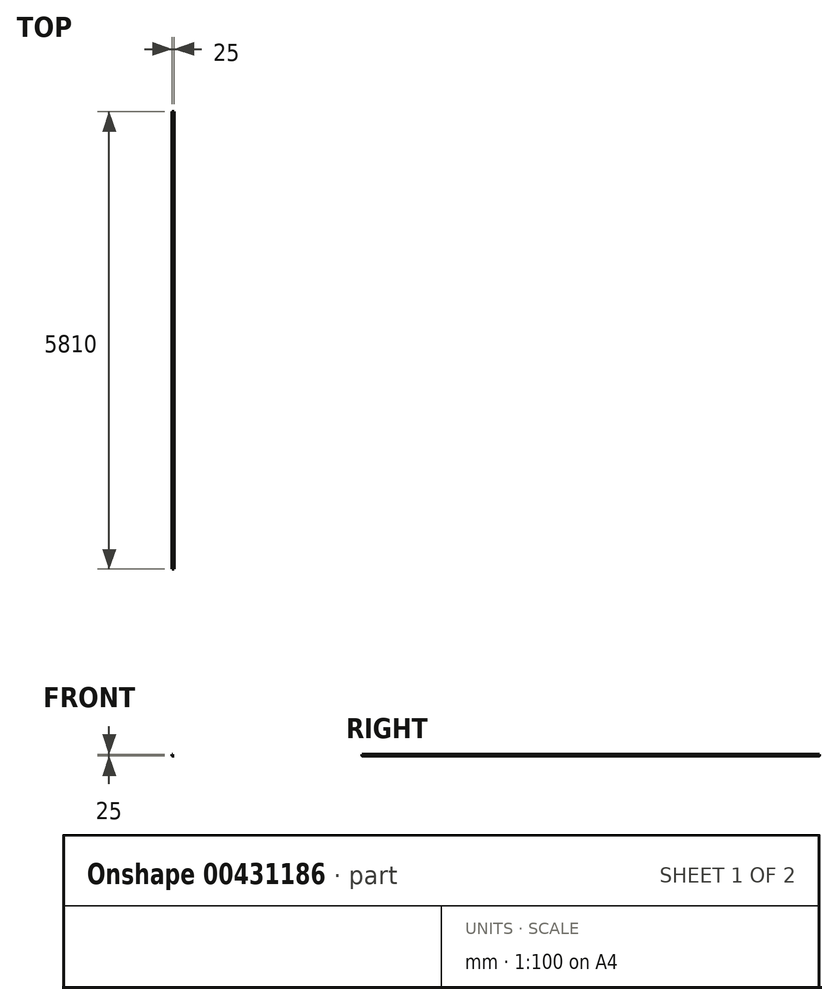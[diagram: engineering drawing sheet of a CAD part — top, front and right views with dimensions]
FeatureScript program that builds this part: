
annotation { "Feature Type Name" : "Feature", "Feature Type Description" : "" }
export const myFeature = defineFeature(function(context is Context, id is Id, definition is map)
    precondition{}
    {
        {
            var Q0;
            Q0=qCreatedBy(makeId("Front.planeOp"),FACE);
            var sketch = newSketch(context, id + "F0", { "sketchPlane" : qUnion([Q0])});
            skLineSegment(sketch, "E0", {"start": v(4.6, 0) * mm, "end": v(25, 0) * mm});
            skLineSegment(sketch, "E1", {"start": v(0, 4.6) * mm, "end": v(0, 25) * mm});
            skLineSegment(sketch, "E2.0", {"start": v(2.3, 4.6) * mm, "end": v(2.3, 25) * mm});
            skLineSegment(sketch, "E3.0", {"start": v(4.6, 2.3) * mm, "end": v(25, 2.3) * mm});
            skLineSegment(sketch, "E4", {"start": v(25, 0) * mm, "end": v(25, 2.3) * mm});
            skLineSegment(sketch, "E5", {"start": v(0, 25) * mm, "end": v(2.3, 25) * mm});
            skPoint(sketch, "E6.visualSharp", {"position": v(2.3, 2.3) * mm});
            skArc(sketch, "E6.filletArc", {"start": v(2.3, 4.6) * mm, "mid": v(2.97, 2.97) * mm, "end": v(4.6, 2.3) * mm});
            skArc(sketch, "E7.0", {"start": v(0, 4.6) * mm, "mid": v(1.35, 1.35) * mm, "end": v(4.6, 0) * mm});
            skSolve(sketch);
        }
        {
            var Q0;
            Q0=makeQuery(id+"F0.imprint","IMPRINT",FACE,{"disambiguationData":[TD([[makeQuery(id+"F0.imprint","IMPRINT",EDGE,{"derivedFrom":sQuery(id+"F0.wireOp",EDGE,"E0")}),1.0]])]});
            extrude(context, id + "F1", {"entities" : qUnion([Q0]), "depth" : 5810 * mm});
        }
    });
